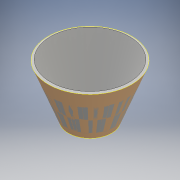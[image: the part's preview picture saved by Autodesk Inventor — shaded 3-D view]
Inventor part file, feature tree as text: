
AUTODESK INVENTOR PART (.ipt)
format: ipt  version: 2016 (Build 200138000, 138)  size: 121,344 bytes
history: native  units: mm
features: sketch x2, plane x1, thicken_offset x1, other x1, loft x1
ambient origin geometry x8: Origin, YZ Plane, XZ Plane, XY Plane, X Axis, Y Axis, Z Axis, Center Point
bodies: Body1 (feature_tree), Body2 (feature_tree)
feature tree (6):
  sketch  "Sketch1"  dims[d0=324.0mm d1=9.52mm]
  plane  "Work Plane1"
  thicken_offset  "Thicken1"
  sketch  "Sketch2"  dims[d2=-203.0mm d3=168.0mm d4=9.52mm d15=0.0mm d16=90.0deg d17=0.0mm d18=90.0deg d19=9.52mm d20=9.52mm]
  other  "Srf1"
  loft  "LoftSrf1"
